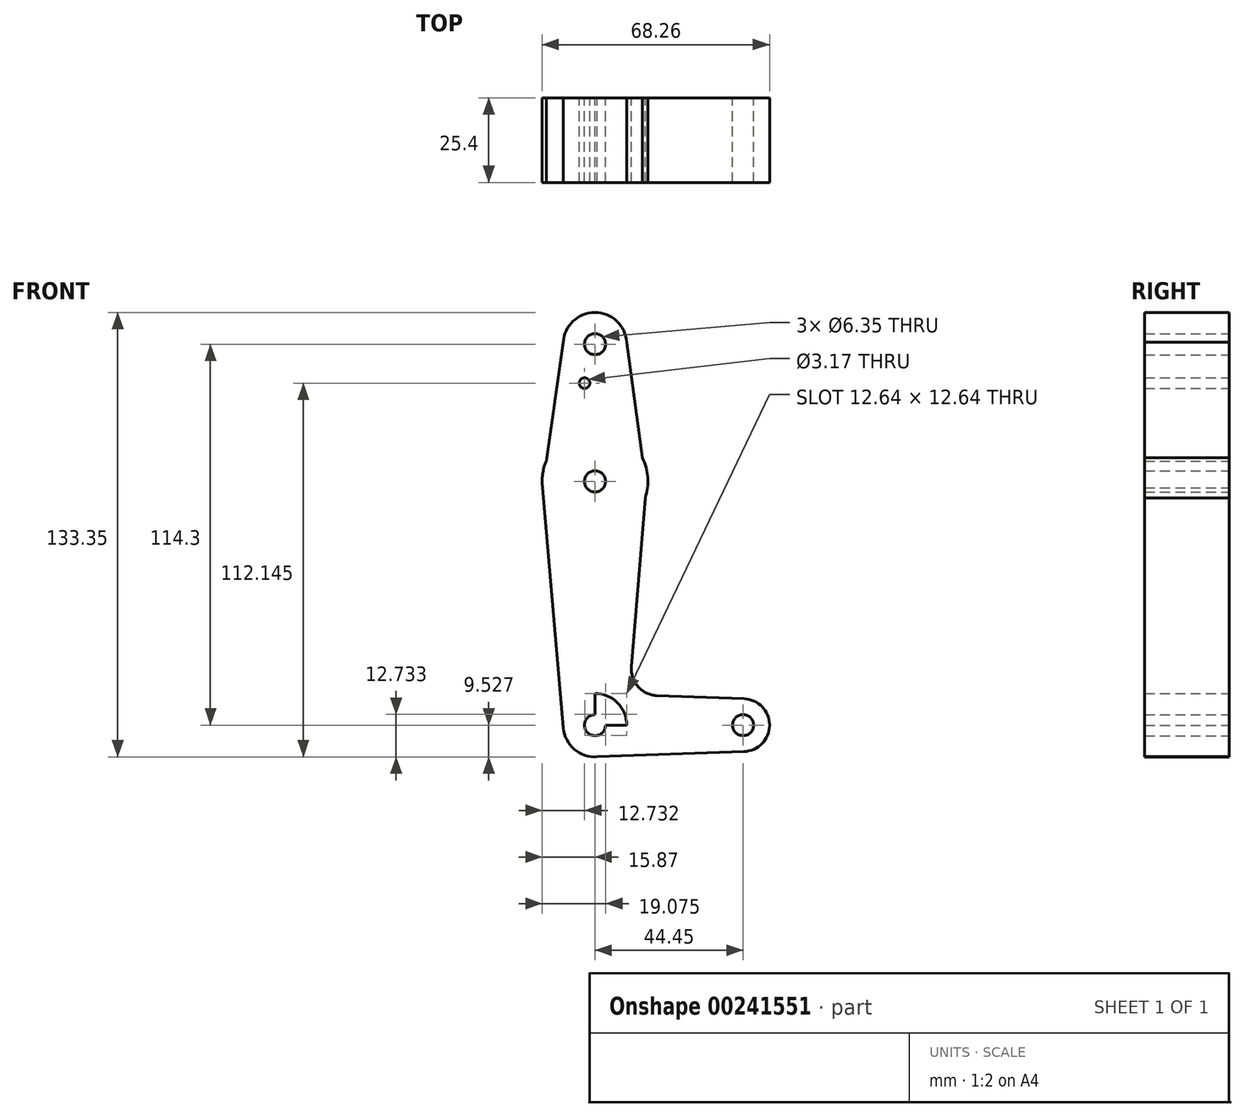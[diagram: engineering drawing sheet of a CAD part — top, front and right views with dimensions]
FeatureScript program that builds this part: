
annotation { "Feature Type Name" : "Feature", "Feature Type Description" : "" }
export const myFeature = defineFeature(function(context is Context, id is Id, definition is map)
    precondition{}
    {
        {
            var Q0;
            Q0=qCreatedBy(makeId("Front.planeOp"),FACE);
            var sketch = newSketch(context, id + "F0", { "sketchPlane" : qUnion([Q0])});
            skLineSegment(sketch, "E0", {"start": v(0, 50.05) * mm, "end": v(0, -64.25) * mm});
            skCircle(sketch, "E1", {"center": v(0, 50.05) * mm, "radius": 9.53 * mm});
            skCircle(sketch, "E2", {"center": v(0, 8.9) * mm, "radius": 15.88 * mm});
            skLineSegment(sketch, "E3", {"start": v(0, -64.25) * mm, "end": v(44.45, -64.25) * mm});
            skCircle(sketch, "E4", {"center": v(44.45, -64.25) * mm, "radius": 7.94 * mm});
            skCircle(sketch, "E5", {"center": v(0, -64.25) * mm, "radius": 9.53 * mm});
            skLineSegment(sketch, "E6", {"start": v(-9.27, 52.22) * mm, "end": v(-14.66, 14.97) * mm});
            skLineSegment(sketch, "E7", {"start": v(9.33, 51.96) * mm, "end": v(14.18, 16.03) * mm});
            skLineSegment(sketch, "E8", {"start": v(-15.76, 6.96) * mm, "end": v(-9.49, -65.08) * mm});
            skLineSegment(sketch, "E9", {"start": v(15.67, 11.42) * mm, "end": v(10.94, -46.8) * mm});
            skLineSegment(sketch, "E10", {"start": v(18.58, -55.39) * mm, "end": v(44.73, -56.32) * mm});
            skLineSegment(sketch, "E11", {"start": v(0, -73.78) * mm, "end": v(44.73, -72.19) * mm});
            skArc(sketch, "E12.filletArc", {"start": v(10.94, -46.8) * mm, "mid": v(12.93, -52.73) * mm, "end": v(18.58, -55.39) * mm});
            skCircle(sketch, "E13", {"center": v(0, 50.05) * mm, "radius": 3.18 * mm});
            skCircle(sketch, "E14", {"center": v(0, 8.9) * mm, "radius": 3.18 * mm});
            skCircle(sketch, "E15", {"center": v(0, -64.25) * mm, "radius": 3.18 * mm});
            skCircle(sketch, "E16", {"center": v(44.45, -64.25) * mm, "radius": 3.18 * mm});
            skCircle(sketch, "E17", {"center": v(-3.14, 38.36) * mm, "radius": 1.59 * mm});
            skSolve(sketch);
        }
        {
            var Q0;
            Q0 = qSketchRegion(id + "F0", true);
            extrude(context, id + "F1", {"entities" : qUnion([Q0]), "depth" : 25.4 * mm});
        }
    });
